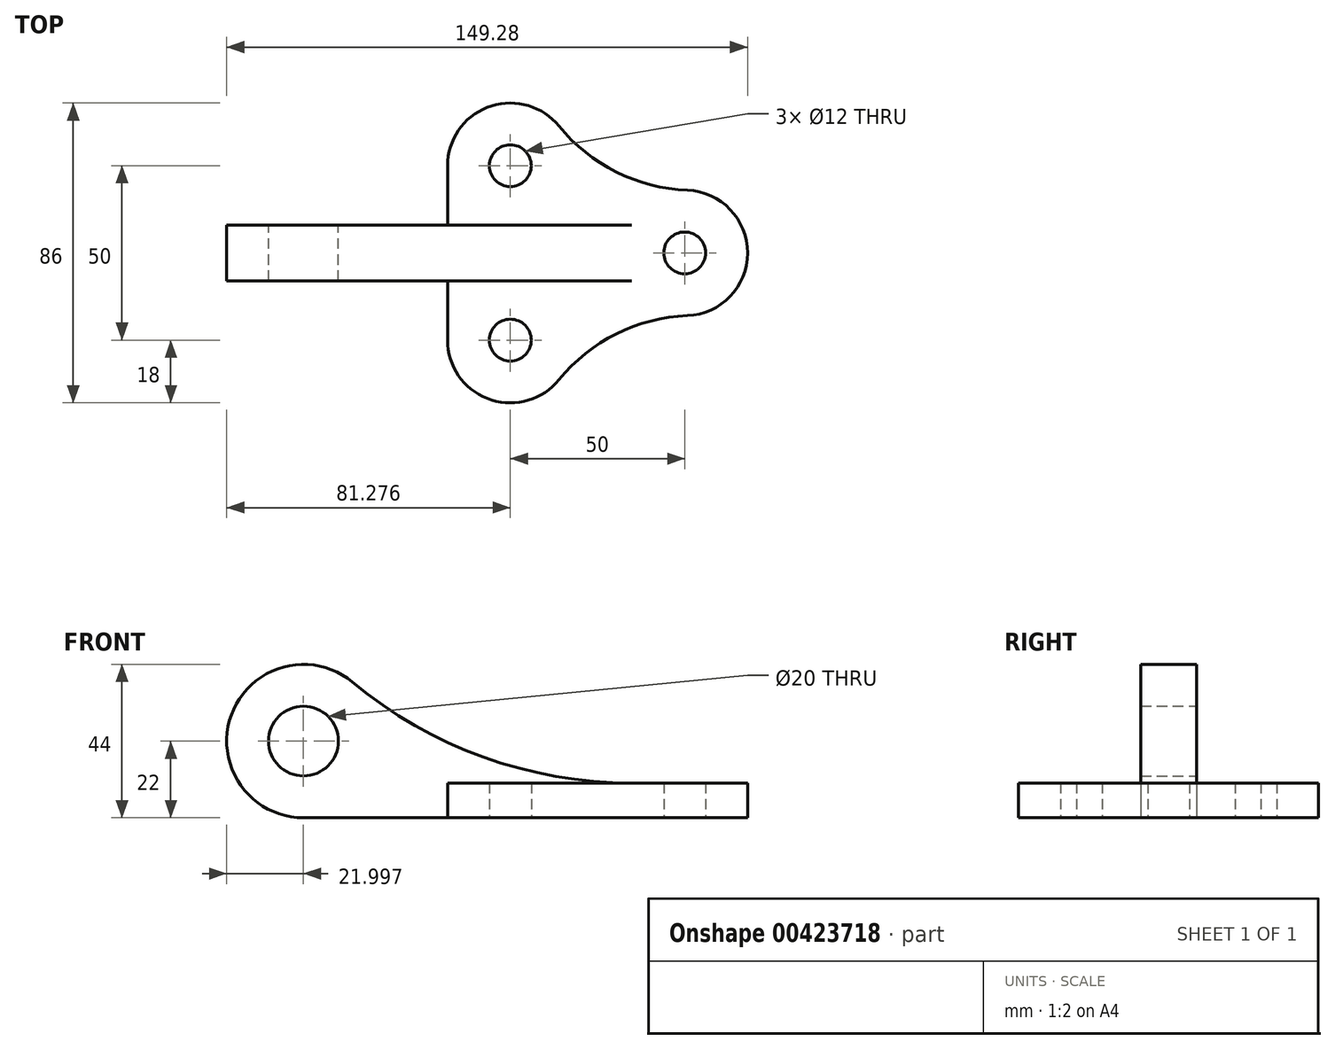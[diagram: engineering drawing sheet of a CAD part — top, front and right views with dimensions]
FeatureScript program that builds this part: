
annotation { "Feature Type Name" : "Feature", "Feature Type Description" : "" }
export const myFeature = defineFeature(function(context is Context, id is Id, definition is map)
    precondition{}
    {
        {
            var Q0;
            Q0=qCreatedBy(makeId("Top.planeOp"),FACE);
            var sketch = newSketch(context, id + "F0", { "sketchPlane" : qUnion([Q0])});
            skCircle(sketch, "E0", {"center": v(33.76, 0) * mm, "radius": 6 * mm});
            skArc(sketch, "E1", {"start": v(34.48, -17.99) * mm, "mid": v(51.76, 0) * mm, "end": v(34.48, 17.99) * mm});
            skCircle(sketch, "E2", {"center": v(-16.24, 25) * mm, "radius": 6 * mm});
            skCircle(sketch, "E3", {"center": v(-16.24, -25) * mm, "radius": 6 * mm});
            skArc(sketch, "E4", {"start": v(-34.2, -23.61) * mm, "mid": v(-22.93, -41.71) * mm, "end": v(-2.29, -36.37) * mm});
            skArc(sketch, "E5", {"start": v(-2.29, 36.37) * mm, "mid": v(-22.93, 41.71) * mm, "end": v(-34.2, 23.61) * mm});
            skLineSegment(sketch, "E6", {"start": v(33.76, 0) * mm, "end": v(105.3, 0) * mm, "construction": true});
            skArc(sketch, "E7", {"start": v(-2.29, 36.37) * mm, "mid": v(14.12, 23.22) * mm, "end": v(34.48, 17.99) * mm});
            skArc(sketch, "E8.MirrorCS", {"start": v(-2.29, -36.37) * mm, "mid": v(14.12, -23.22) * mm, "end": v(34.48, -17.99) * mm});
            skLineSegment(sketch, "E9", {"start": v(-34.2, 26.39) * mm, "end": v(-34.2, -26.39) * mm});
            skSolve(sketch);
        }
        {
            var Q0;
            Q0=makeQuery(id+"F0.imprint","IMPRINT",FACE,{"disambiguationData":[TD([[makeQuery(id+"F0.imprint","IMPRINT",EDGE,{"derivedFrom":sQuery(id+"F0.wireOp",EDGE,"E0")}),-1.0]])]});
            extrude(context, id + "F1", {"entities" : qUnion([Q0]), "depth" : 10 * mm});
        }
        {
            var Q0;
            Q0=qCreatedBy(makeId("Front.planeOp"),FACE);
            var sketch = newSketch(context, id + "F2", { "sketchPlane" : qUnion([Q0])});
            skLineSegment(sketch, "E10.0", {"start": v(34.48, 10) * mm, "end": v(34.48, 0) * mm, "construction": true});
            skLineSegment(sketch, "E11", {"start": v(18.5, 0) * mm, "end": v(-75.52, 0) * mm});
            skArc(sketch, "E12", {"start": v(-61.45, 38.91) * mm, "mid": v(-96.21, 29.48) * mm, "end": v(-75.52, 0) * mm});
            skCircle(sketch, "E13", {"center": v(-75.52, 22) * mm, "radius": 10 * mm});
            skLineSegment(sketch, "E14.0", {"start": v(-2.29, 10) * mm, "end": v(18.5, 10) * mm});
            skArc(sketch, "E15", {"start": v(-61.45, 38.91) * mm, "mid": v(-24.01, 17.45) * mm, "end": v(18.5, 10) * mm});
            skLineSegment(sketch, "E16", {"start": v(18.5, 10) * mm, "end": v(18.5, 0) * mm});
            skSolve(sketch);
        }
        {
            var Q0;
            Q0=makeQuery(id+"F2.imprint","IMPRINT",FACE,{"disambiguationData":[TD([[makeQuery(id+"F2.imprint","IMPRINT",EDGE,{"derivedFrom":sQuery(id+"F2.wireOp",EDGE,"E11")}),-1.0]])]});
            extrude(context, id + "F3", {"entities" : qUnion([Q0]), "operationType" : NewBodyOperationType.ADD, "endBound" : BoundingType.SYMMETRIC, "depth" : 16 * mm});
        }
    });
